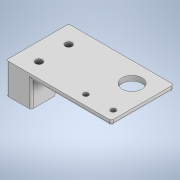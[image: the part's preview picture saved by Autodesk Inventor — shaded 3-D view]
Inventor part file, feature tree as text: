
AUTODESK INVENTOR PART (.ipt)
format: ipt  version: 2022.3 (Build 263350000, 350)  size: 192,000 bytes
history: native  units: in
note: dims shown in document units (in); Inventor stores cm internally (conversion verified against a paired STEP export)
features: extrude x7, sketch x7, fillet x1
ambient origin geometry x8: Origin, YZ Plane, XZ Plane, XY Plane, X Axis, Y Axis, Z Axis, Center Point
bodies: Solid1 (feature_tree)
feature tree (15):
  extrude  "Extrusion1"  Depth=2.65in
  extrude  "Extrusion2"  Depth=0.125in
  extrude  "Extrusion3"  Depth=0.625in
  extrude  "Extrusion4"  Depth=0.65in
  extrude  "Extrusion5"  Depth=0.25in
  extrude  "Extrusion6"  Depth=0.375in
  fillet  "Fillet1"  Radius=0.1in
  extrude  "Extrusion7"  Depth=0.375in
  sketch  "Sketch1"  dims[d0=1.575in d1=2.65in]
  sketch  "Sketch2"  dims[d2=0.125in d3=0.0in d4=0.55in]
  sketch  "Sketch3"  dims[d6=0.25in d7=0.0in d8=0.625in]
  sketch  "Sketch4"  dims[d9=0.65in d10=0.0in d11=0.5in]
  sketch  "Sketch5"  dims[d12=0.25in d13=0.0in d14=0.63in]
  sketch  "Sketch6"  dims[d15=0.25in d16=0.375in d17=0.1in d18=0.0in]
  sketch  "Sketch7"  dims[d19=0.1719in d20=0.1719in d21=0.45in d22=0.45in d23=0.75in d24=0.375in d25=1.0in d26=0.0in d27=0.05in d28=0.5in d29=0.5in d30=0.125in d31=0.125in d32=0.2in d33=0.6929in d34=0.25in d35=0.25in d36=1.0in d37=0.0in d38=0.375in]
